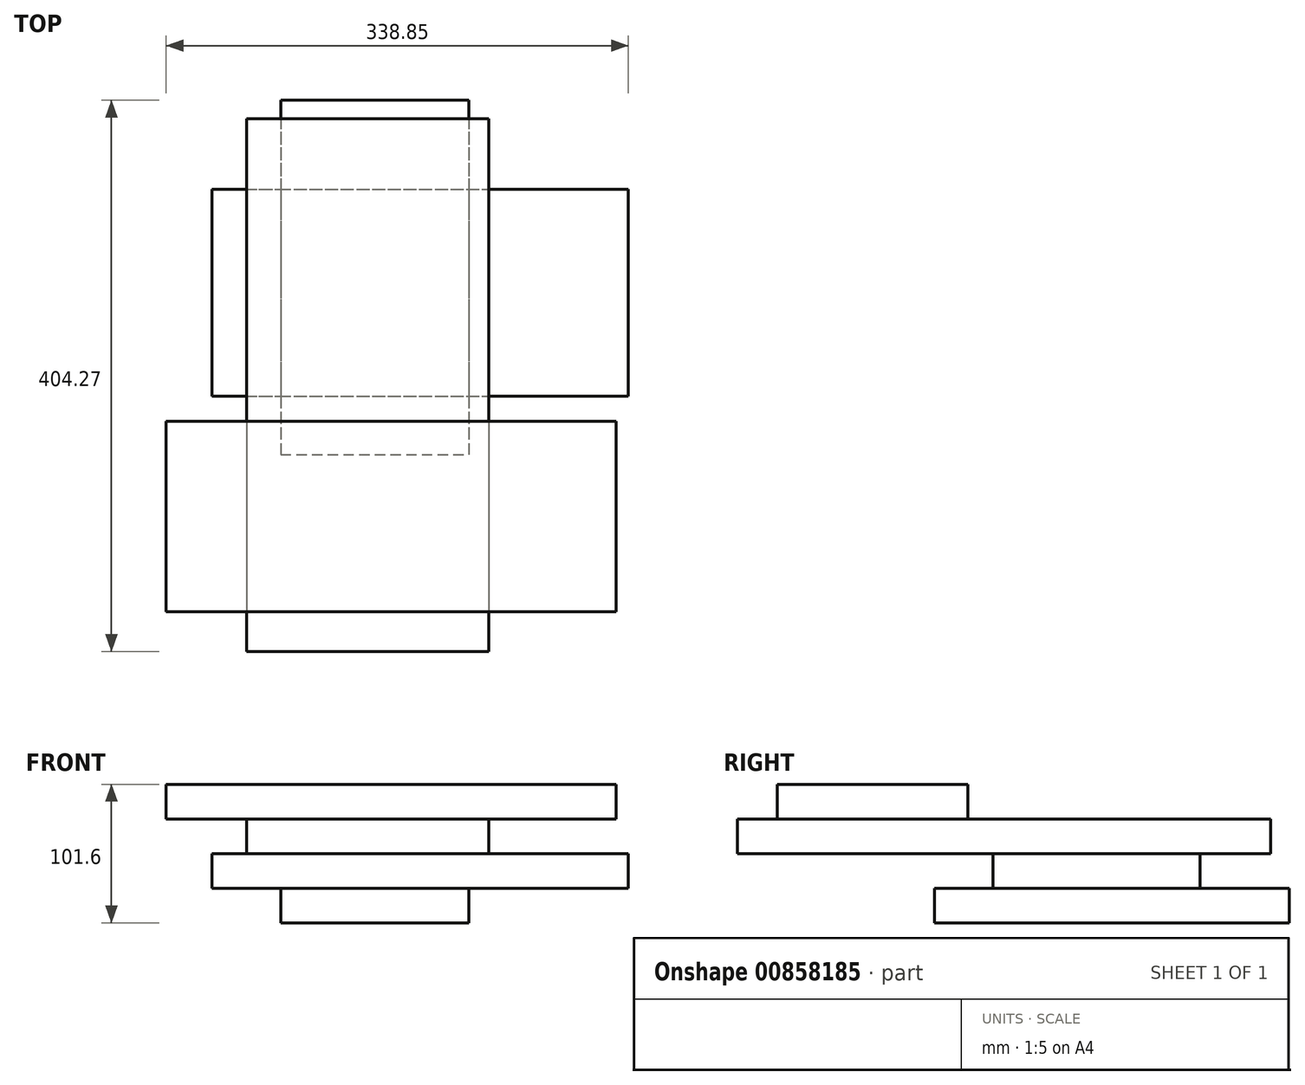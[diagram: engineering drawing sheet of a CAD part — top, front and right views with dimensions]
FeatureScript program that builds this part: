
annotation { "Feature Type Name" : "Feature", "Feature Type Description" : "" }
export const myFeature = defineFeature(function(context is Context, id is Id, definition is map)
    precondition{}
    {
        {
            var Q0;
            Q0=qCreatedBy(makeId("Top.planeOp"),FACE);
            var sketch = newSketch(context, id + "F0", { "sketchPlane" : qUnion([Q0])});
            skLineSegment(sketch, "E0.bottom", {"start": v(-91.4, 57.44) * mm, "end": v(46.6, 57.44) * mm});
            skLineSegment(sketch, "E0.top", {"start": v(-91.4, -202.39) * mm, "end": v(46.6, -202.39) * mm});
            skLineSegment(sketch, "E0.left", {"start": v(-91.4, 57.44) * mm, "end": v(-91.4, -202.39) * mm});
            skLineSegment(sketch, "E0.right", {"start": v(46.6, 57.44) * mm, "end": v(46.6, -202.39) * mm});
            skSolve(sketch);
        }
        {
            var Q0;
            Q0 = qSketchRegion(id + "F0", true);
            extrude(context, id + "F1", {"entities" : qUnion([Q0]), "depth" : 25.4 * mm, "offsetDistance" : 25.4 * mm});
        }
        {
            var Q0;
            Q0=makeQuery(id+"F1.opExtrude","CAP_FACE",FACE,{"disambiguationData":[OSD([sQuery(id+"F0.wireOp",EDGE,"E0.bottom"),sQuery(id+"F0.wireOp",EDGE,"E0.top"),sQuery(id+"F0.wireOp",EDGE,"E0.left"),sQuery(id+"F0.wireOp",EDGE,"E0.right")])],"isStart":false});
            var sketch = newSketch(context, id + "F2", { "sketchPlane" : qUnion([Q0])});
            skLineSegment(sketch, "E1.bottom", {"start": v(-141.94, -7.92) * mm, "end": v(163.45, -7.92) * mm});
            skLineSegment(sketch, "E1.top", {"start": v(-141.94, -159.61) * mm, "end": v(163.45, -159.61) * mm});
            skLineSegment(sketch, "E1.left", {"start": v(-141.94, -7.92) * mm, "end": v(-141.94, -159.61) * mm});
            skLineSegment(sketch, "E1.right", {"start": v(163.45, -7.92) * mm, "end": v(163.45, -159.61) * mm});
            skSolve(sketch);
        }
        {
            var Q0;
            Q0 = qSketchRegion(id + "F2", true);
            extrude(context, id + "F3", {"entities" : qUnion([Q0]), "operationType" : NewBodyOperationType.ADD, "depth" : 25.4 * mm, "offsetDistance" : 25.4 * mm});
        }
        {
            var Q0;
            Q0=makeQuery(id+"F3.opExtrude","CAP_FACE",FACE,{"disambiguationData":[OSD([sQuery(id+"F2.wireOp",EDGE,"E1.bottom"),sQuery(id+"F2.wireOp",EDGE,"E1.top"),sQuery(id+"F2.wireOp",EDGE,"E1.left"),sQuery(id+"F2.wireOp",EDGE,"E1.right")])],"isStart":false});
            var sketch = newSketch(context, id + "F4", { "sketchPlane" : qUnion([Q0])});
            skLineSegment(sketch, "E2.bottom", {"start": v(-116.41, 43.77) * mm, "end": v(61.05, 43.77) * mm});
            skLineSegment(sketch, "E2.top", {"start": v(-116.41, -346.83) * mm, "end": v(61.05, -346.83) * mm});
            skLineSegment(sketch, "E2.left", {"start": v(-116.41, 43.77) * mm, "end": v(-116.41, -346.83) * mm});
            skLineSegment(sketch, "E2.right", {"start": v(61.05, 43.77) * mm, "end": v(61.05, -346.83) * mm});
            skSolve(sketch);
        }
        {
            var Q0;
            Q0 = qSketchRegion(id + "F4", true);
            extrude(context, id + "F5", {"entities" : qUnion([Q0]), "operationType" : NewBodyOperationType.ADD, "depth" : 25.4 * mm, "offsetDistance" : 25.4 * mm});
        }
        {
            var Q0;
            Q0=makeQuery(id+"F5.opExtrude","CAP_FACE",FACE,{"disambiguationData":[OSD([sQuery(id+"F4.wireOp",EDGE,"E2.bottom"),sQuery(id+"F4.wireOp",EDGE,"E2.top"),sQuery(id+"F4.wireOp",EDGE,"E2.left"),sQuery(id+"F4.wireOp",EDGE,"E2.right")])],"isStart":false});
            var sketch = newSketch(context, id + "F6", { "sketchPlane" : qUnion([Q0])});
            skSolve(sketch);
        }
        {
            var Q0;
            Q0=makeQuery(id+"F6.imprint","IMPRINT",FACE,{"disambiguationData":[TD([[makeQuery(id+"F6.imprint","IMPRINT",EDGE,{"derivedFrom":makeQuery(id+"F5.opExtrude","CAP_EDGE",EDGE,{"disambiguationData":[OSD([sQuery(id+"F4.wireOp",EDGE,"E2.bottom")])],"isStart":false})}),-1.0]])]});
            var sketch = newSketch(context, id + "F7", { "sketchPlane" : qUnion([Q0])});
            skLineSegment(sketch, "E3.bottom", {"start": v(-175.4, -177.93) * mm, "end": v(154.4, -177.93) * mm});
            skLineSegment(sketch, "E3.top", {"start": v(-175.4, -317.62) * mm, "end": v(154.4, -317.62) * mm});
            skLineSegment(sketch, "E3.left", {"start": v(-175.4, -177.93) * mm, "end": v(-175.4, -317.62) * mm});
            skLineSegment(sketch, "E3.right", {"start": v(154.4, -177.93) * mm, "end": v(154.4, -317.62) * mm});
            skSolve(sketch);
        }
        {
            var Q0;
            Q0 = qSketchRegion(id + "F7", true);
            extrude(context, id + "F8", {"entities" : qUnion([Q0]), "operationType" : NewBodyOperationType.ADD, "depth" : 25.4 * mm, "offsetDistance" : 25.4 * mm});
        }
    });
